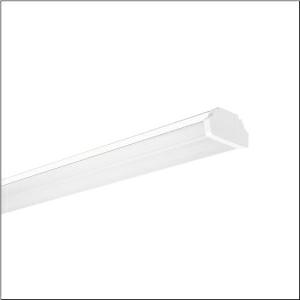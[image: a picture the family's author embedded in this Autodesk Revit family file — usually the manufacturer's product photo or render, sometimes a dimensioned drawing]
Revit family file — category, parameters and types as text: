
# Revit family: modario_31_gen_2_53bm812dv4d5d2_bcfa
name_source: partatom
category: Lighting Fixtures
units: mm (PartAtom-declared; Revit-internal decimal feet)

## family parameters
Cut with Voids When Loaded = No
Host = Face
Light Source = No
Part Type = Normal
Room Calculation Point = No
Round Connector Dimension = Use Diameter
Shared = No

## types (1)
- --- (1 x LED, 13680 lm, 74.9 W, 4000K)
    Apparent Load = 75 VA
    CIE Flux Codes = 47 80 95 93 100
    Color Rendering = 80
    Color Temperature = 4000K
    Default Elevation = 1800 mm
    Description = Modario 31 Gen.2, luminaire insert, of sheet steel, coil coated, white, length: 1.495mm, width: 81mm, height: 82mm, 5x system unit, system units: 299mm, LED rated luminous flux: 13.680lm, light colour: 840, SDCM (Standard Deviation of Colour Matching)MacAdam ≤ 3 SDCM (initial), control gear: DALI 2, control gear: ECG DALI, with plug, 5-pole, with phase selection, mains connection: 220..240V, AC, 50/60Hz, rated input power: 75W, through-wiring accessed according to module size, primary optical cover: cover, of PMMA, light emission: direct distribution, primary light characteristic: symmetric, protection rating (complete): IP20, protection rating (LED compartment): IP50, insulation class (complete): insulation class I (protective earthing), certification: CE, ENEC, VDE, UKCA, impact resistance: IK03, permissible ambient temperature for indoor applications: -25..+35°C, corresponds to IFS (International Featured Standards) requirements for safety and quality in the food industry, reducing of maximum allowable ambient temperature of 5°C with ceiling mounting, IP40 when using the optional accessory 5TP9018, packaging unit: 1 piece
    Height = 92 mm
    Lamp = 1 x LED
    Lamp Light Flux = 13680 lm
    Lamp Power = 74.9 W
    Lamp count = 1
    Length = 1495 mm
    Luminous efficacy = 183 lm/W
    Manufacturer = Siteco
    ModVariant = No
    Model = 53BM812DV4D5D2
    Mounting Place = Ceiling
    Mounting Type = Pendant
    Number of Poles = 1
    OnlyDefault = Yes
    Power Factor = 1
    Product Name = Modario 31 Gen.2
    Product group = luminaire insert | ceiling pendant
    ProductGroupID = 901
    Protection Class = Protection class I
    Protection Degree = IP 20
    RLX_Detail_Level = 1
    RLX_Emergency_Light_Flux = 0 lm
    RLX_Emergency_Type = 0
    RLX_Emergency_Type_DB = No
    RlxData = <blob elided: 42169 chars, md5=d8b4196b>
    Socket = socket
    Standby Power = 0 W
    System Light Flux = 13680 lm
    System Power = 75 W
    Type Comments = factory setting: luminous flux: 100 % | dim-lin: 254 | 511 mA
    Type Image = l_1341886.jpg
    URL = http://relux.com
    VarID = @adj_052665
    Voltage = 0 V
    Weight = 0.00 kg
    Width = 81 mm

## geometry (parser evidence)
native form markers: Blend x4, Sweep x12
no freeform markers — native parametric forms only
